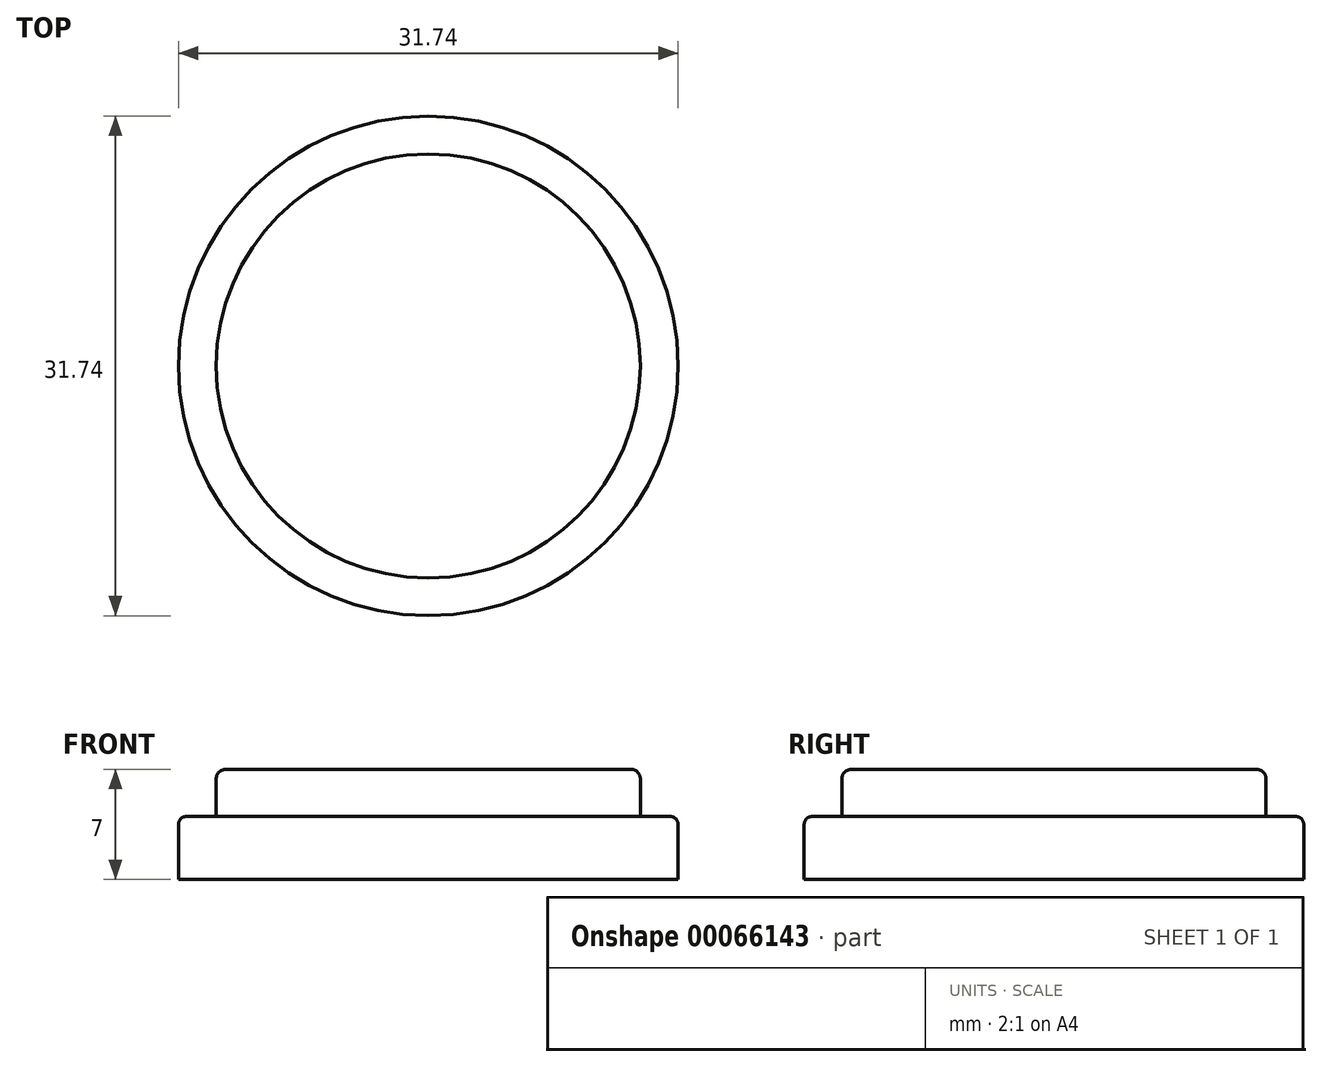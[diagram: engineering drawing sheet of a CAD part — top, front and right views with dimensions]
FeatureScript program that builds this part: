
annotation { "Feature Type Name" : "Feature", "Feature Type Description" : "" }
export const myFeature = defineFeature(function(context is Context, id is Id, definition is map)
    precondition{}
    {
        {
            var Q0;
            Q0=qCreatedBy(makeId("Top.planeOp"),FACE);
            var sketch = newSketch(context, id + "F0", { "sketchPlane" : qUnion([Q0])});
            skCircle(sketch, "E0", {"center": v(0, 0) * mm, "radius": 13.47 * mm});
            skSolve(sketch);
        }
        {
            var Q0;
            Q0 = qSketchRegion(id + "F0", true);
            extrude(context, id + "F1", {"entities" : qUnion([Q0]), "depth" : 7 * mm});
        }
        {
            var Q0;
            Q0=makeQuery(id+"F1.opExtrude","CAP_FACE",FACE,{"disambiguationData":[OSD([sQuery(id+"F0.wireOp",EDGE,"E0")])],"isStart":false});
            fillet(context, id + "F2", {"entities" : qUnion([Q0]), "radius" : 0.6 * mm, "tangentPropagation" : true, "allowEdgeOverflow" : false});
        }
        {
            var Q0;
            Q0=qCreatedBy(makeId("Top.planeOp"),FACE);
            var sketch = newSketch(context, id + "F3", { "sketchPlane" : qUnion([Q0])});
            skCircle(sketch, "E1", {"center": v(0, 0) * mm, "radius": 15.87 * mm});
            skSolve(sketch);
        }
        {
            var Q0;
            Q0 = qSketchRegion(id + "F3", true);
            extrude(context, id + "F4", {"entities" : qUnion([Q0]), "operationType" : NewBodyOperationType.ADD, "depth" : 4 * mm});
        }
        {
            var Q0;
            Q0=makeQuery(id+"F4.opExtrude","CAP_EDGE",EDGE,{"disambiguationData":[OSD([sQuery(id+"F3.wireOp",EDGE,"E1")])],"isStart":false});
            fillet(context, id + "F5", {"entities" : qUnion([Q0]), "radius" : 0.5 * mm, "tangentPropagation" : true, "allowEdgeOverflow" : false});
        }
    });
